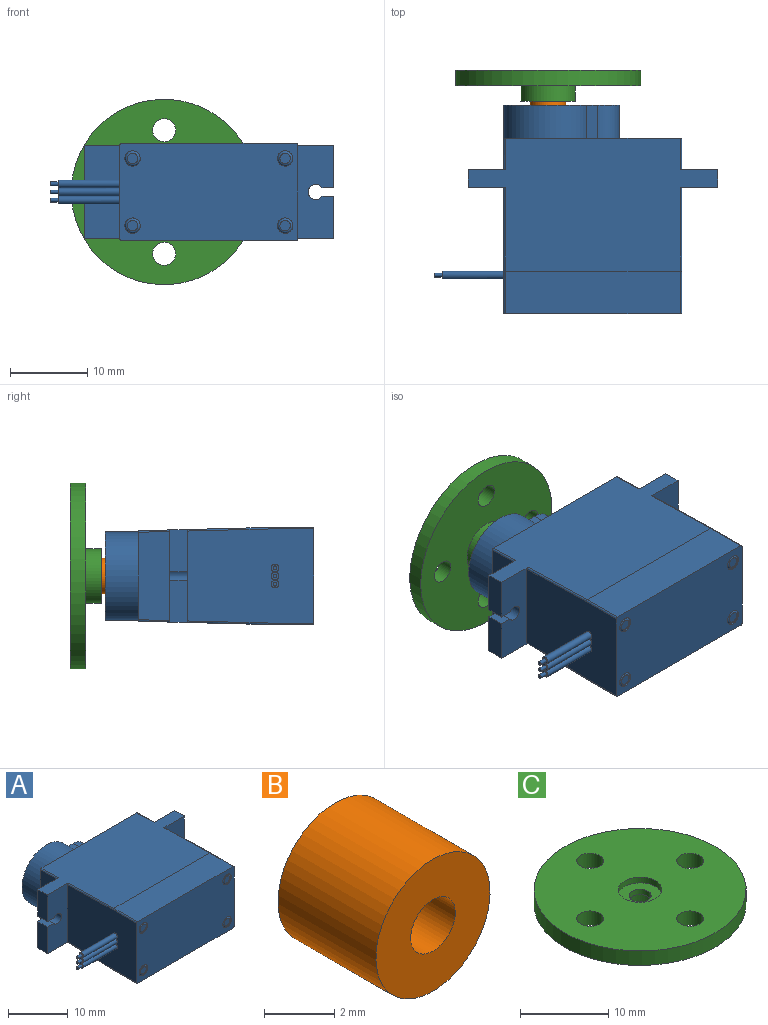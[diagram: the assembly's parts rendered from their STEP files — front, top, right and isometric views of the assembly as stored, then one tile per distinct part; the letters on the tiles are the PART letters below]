
ASSEMBLY  parts=3 mates=1
PART A: 75 faces, bbox 36.7x27x12.6 mm
  f0: plane 23.03x12.59mm, normal (0,-1,0), area 277.3mm2, adj f12,f25,f27,f29,f31,f39,f46,f49
  f1: plane 5.48x2.32mm, normal (-1,0,0), area 12.6mm2, adj f2,f4,f45,f74
  f2: plane 11.93x4.84mm, normal (0,1,0), area 50.8mm2, adj f1,f3,f4,f5,f35,f36,f45,f50
  f3: cylinder r=0.97mm len=2.32mm, axis (0,1,0), area 11.5mm2, adj f2,f4,f5,f74
  f4: plane 2.32x1.51mm, normal (0,0,1), area 3.5mm2, adj f1,f2,f3,f74
  f5: plane 2.32x1.51mm, normal (0,0,-1), area 3.5mm2, adj f2,f3,f50,f74
  f6: plane 11.93x4.84mm, normal (0,1,0), area 50.8mm2, adj f7,f33,f34,f45,f47,f48,f53,f54
  f7: plane 5.48x2.32mm, normal (1,0,0), area 12.6mm2, adj f6,f8,f53,f55
  f8: plane 12.04x4.84mm, normal (0,-1,0), area 51.4mm2, adj f7,f30,f32,f45,f48,f49,f53,f54
  f9: plane 1x1mm, normal (-1,0,0), area 0.6mm2, adj f14,f19
  f10: plane 1x1mm, normal (-1,0,0), area 0.6mm2, adj f13,f17
  f11: plane 1x1mm, normal (-1,0,0), area 0.6mm2, adj f15,f70
  f12: plane 16.34x12.19mm, normal (-1,0,0), area 193.9mm2, adj f0,f13,f14,f25,f26,f27,f28,f70
  f13: cylinder r=0.5mm len=8mm, axis (-1,0,0), area 25.1mm2, adj f10,f12
  f14: cylinder r=0.5mm len=8mm, axis (-1,0,0), area 25.1mm2, adj f9,f12
  f15: cylinder r=0.25mm len=1mm, axis (-1,0,0), area 1.6mm2, adj f11,f16
  f16: plane 0.5x0.5mm, normal (-1,0,0), area 0.2mm2, adj f15
  f17: cylinder r=0.25mm len=1mm, axis (-1,0,0), area 1.6mm2, adj f10,f18
  f18: plane 0.5x0.5mm, normal (-1,0,0), area 0.2mm2, adj f17
  f19: cylinder r=0.25mm len=1mm, axis (-1,0,0), area 1.6mm2, adj f9,f20
  f20: plane 0.5x0.5mm, normal (-1,0,0), area 0.2mm2, adj f19
  f21: torus R=0.68mm, axis (0,1,0), area 2.6mm2, adj f64,f65
  f22: torus R=0.68mm, axis (0,1,0), area 2.6mm2, adj f68,f69
  f23: torus R=0.68mm, axis (0,1,0), area 2.6mm2, adj f60,f61
  f24: torus R=0.68mm, axis (0,1,0), area 2.6mm2, adj f57,f71
  f25: cylinder r=0.2mm len=5.5mm, axis (0,-1,0), area 1.7mm2, adj f0,f12,f26,f46
  f26: cylinder r=0.2mm len=10.85mm, axis (0,-1,0.03), area 3.4mm2, adj f12,f25,f53,f74
  f27: cylinder r=0.2mm len=5.5mm, axis (0,1,0), area 1.7mm2, adj f0,f12,f28,f39
  f28: cylinder r=0.2mm len=10.85mm, axis (0,1,0.03), area 3.4mm2, adj f12,f27,f45,f74
  f29: cylinder r=0.2mm len=5.5mm, axis (0,1,0), area 1.7mm2, adj f0,f30,f46,f49
  f30: cylinder r=0.2mm len=10.85mm, axis (0,1,-0.03), area 3.4mm2, adj f8,f29,f49,f53
  f31: cylinder r=0.2mm len=5.5mm, axis (0,-1,0), area 1.7mm2, adj f0,f32,f39,f49
  f32: cylinder r=0.2mm len=10.85mm, axis (0,-1,-0.03), area 3.4mm2, adj f8,f31,f45,f49
  f33: cylinder r=0.2mm len=4.07mm, axis (0,-1,-0.03), area 1.3mm2, adj f6,f45,f47,f52
  f34: cylinder r=0.2mm len=4.07mm, axis (0,1,-0.03), area 1.3mm2, adj f6,f47,f52,f53
  f35: cylinder r=0.2mm len=4.07mm, axis (0,1,0.03), area 1.3mm2, adj f2,f45,f51,f52
  f36: cylinder r=0.2mm len=4.07mm, axis (0,-1,0.03), area 1.3mm2, adj f2,f51,f52,f53
  f37: cylinder r=2.35mm len=4.7mm, axis (0,-1,0), area 30.3mm2, adj f38,f44
  f38: plane 4.7x4.7mm, normal (0,1,0), area 17.3mm2, adj f37
  f39: plane 22.63x5.5mm, normal (0,0,-1), area 124.5mm2, adj f0,f27,f31,f45
  f40: cylinder r=5.72mm len=11.45mm, axis (0,1,0), area 128.4mm2, adj f41,f43,f44,f52
  f41: plane 4.28x1.41mm, normal (0,0,1), area 6mm2, adj f40,f42,f44,f52
  f42: cylinder r=2.85mm len=5.7mm, axis (0,1,0), area 38.3mm2, adj f41,f43,f44,f52
  f43: plane 4.28x1.41mm, normal (0,0,-1), area 6mm2, adj f40,f42,f44,f52
  f44: plane 14.95x11.45mm, normal (0,1,0), area 103.5mm2, adj f37,f40,f41,f42,f43
  f45: plane 32.31x17.22mm, normal (0,0.03,-1), area 412.3mm2, adj f1,f2,f6,f8,f28,f32,f33,f35
  f46: plane 22.63x5.5mm, normal (0,0,1), area 124.5mm2, adj f0,f25,f29,f53
  f47: plane 11.53x4.06mm, normal (1,0,0), area 46.4mm2, adj f6,f33,f34,f52
  f48: plane 5.48x2.32mm, normal (1,0,0), area 12.6mm2, adj f6,f8,f45,f56
  f49: plane 16.34x12.19mm, normal (1,0,0), area 196.2mm2, adj f0,f8,f29,f30,f31,f32
  f50: plane 5.48x2.32mm, normal (-1,0,0), area 12.6mm2, adj f2,f5,f53,f74
  f51: plane 11.53x4.06mm, normal (-1,0,0), area 46.4mm2, adj f2,f35,f36,f52
  f52: plane 23.03x11.72mm, normal (0,1,0), area 149mm2, adj f33,f34,f35,f36,f40,f41,f42,f43
  f53: plane 32.31x17.22mm, normal (0,0.03,1), area 412.3mm2, adj f2,f6,f7,f8,f26,f30,f34,f36
  f54: cylinder r=0.97mm len=2.32mm, axis (0,1,0), area 11.5mm2, adj f6,f8,f55,f56
  f55: plane 2.32x1.51mm, normal (0,0,-1), area 3.5mm2, adj f6,f7,f8,f54
  f56: plane 2.32x1.51mm, normal (0,0,1), area 3.5mm2, adj f6,f8,f48,f54
  f57: plane 1.35x1.35mm, normal (0,-1,0), area 1.4mm2, adj f24
  f58: cylinder r=1mm len=2mm, axis (0,1,0), area 6.3mm2, adj f0,f59
  f59: plane 2x2mm, normal (0,-1,0), area 0.2mm2, adj f58,f60
  f60: cylinder r=0.97mm len=1.95mm, axis (0,1,0), area 4.3mm2, adj f23,f59
  f61: plane 1.35x1.35mm, normal (0,-1,0), area 1.4mm2, adj f23
  f62: cylinder r=1mm len=2mm, axis (0,1,0), area 6.3mm2, adj f0,f63
  f63: plane 2x2mm, normal (0,-1,0), area 0.2mm2, adj f62,f64
  f64: cylinder r=0.97mm len=1.95mm, axis (0,1,0), area 4.3mm2, adj f21,f63
  f65: plane 1.35x1.35mm, normal (0,-1,0), area 1.4mm2, adj f21
  f66: cylinder r=1mm len=2mm, axis (0,1,0), area 6.3mm2, adj f0,f67
  f67: plane 2x2mm, normal (0,-1,0), area 0.2mm2, adj f66,f68
  f68: cylinder r=0.97mm len=1.95mm, axis (0,1,0), area 4.3mm2, adj f22,f67
  f69: plane 1.35x1.35mm, normal (0,-1,0), area 1.4mm2, adj f22
  f70: cylinder r=0.5mm len=8mm, axis (-1,0,0), area 25.1mm2, adj f11,f12
  f71: cylinder r=0.97mm len=1.95mm, axis (0,1,0), area 4.3mm2, adj f24,f72
  f72: plane 2x2mm, normal (0,-1,0), area 0.2mm2, adj f71,f73
  f73: cylinder r=1mm len=2mm, axis (0,1,0), area 6.3mm2, adj f0,f72
  f74: plane 12.04x4.84mm, normal (0,-1,0), area 51.4mm2, adj f1,f3,f4,f5,f12,f26,f28,f45
PART B: 4 faces, bbox 4.6x4x4.6 mm
  f0: cylinder r=2.3mm len=4.6mm, axis (0,1,0), area 57.1mm2, adj f1,f3
  f1: plane 4.6x4.6mm, normal (0,-1,0), area 14.1mm2, adj f0,f2
  f2: cylinder r=0.9mm len=3.95mm, axis (0,1,0), area 22.3mm2, adj f1,f3
  f3: plane 4.6x4.6mm, normal (0,1,0), area 14.1mm2, adj f0,f2
PART C: 14 faces, bbox 24x24x4 mm
  f0: cylinder r=3.54mm len=7.07mm, axis (0,0,-1), area 44.4mm2, adj f1,f3
  f1: plane 7.07x7.07mm, normal (0,0,-1), area 21.5mm2, adj f0,f13
  f2: cylinder r=12mm len=24mm, axis (0,0,1), area 150.8mm2, adj f3,f4
  f3: plane 24x24mm, normal (0,0,-1), area 384.9mm2, adj f0,f2,f8,f9,f10,f11
  f4: plane 24x24mm, normal (0,0,1), area 404.9mm2, adj f2,f5,f8,f9,f10,f11
  f5: cylinder r=2.48mm len=4.95mm, axis (0,0,1), area 12.4mm2, adj f4,f6
  f6: plane 4.95x4.95mm, normal (0,0,1), area 14.4mm2, adj f5,f7
  f7: cylinder r=1.25mm len=2.49mm, axis (0,0,1), area 5.9mm2, adj f6,f12
  f8: cylinder r=1.5mm len=3mm, axis (0,0,1), area 18.8mm2, adj f3,f4
  f9: cylinder r=1.5mm len=3mm, axis (0,0,1), area 18.8mm2, adj f3,f4
  f10: cylinder r=1.5mm len=3mm, axis (0,0,1), area 18.8mm2, adj f3,f4
  f11: cylinder r=1.5mm len=3mm, axis (0,0,1), area 18.8mm2, adj f3,f4
  f12: plane 4.75x4.75mm, normal (0,0,-1), area 12.9mm2, adj f7,f13
  f13: cylinder r=2.38mm len=4.75mm, axis (0,0,-1), area 36.6mm2, adj f1,f12
PLACE A at identity
PLACE B at identity
PLACE C rot(axis=(-1,0,0),90deg) t=(-1.4,11.16,0)mm
MATE fastened C.f7 <-> B.f0  axis (0,-1,0) through (-1.4,13.61,0)mm
